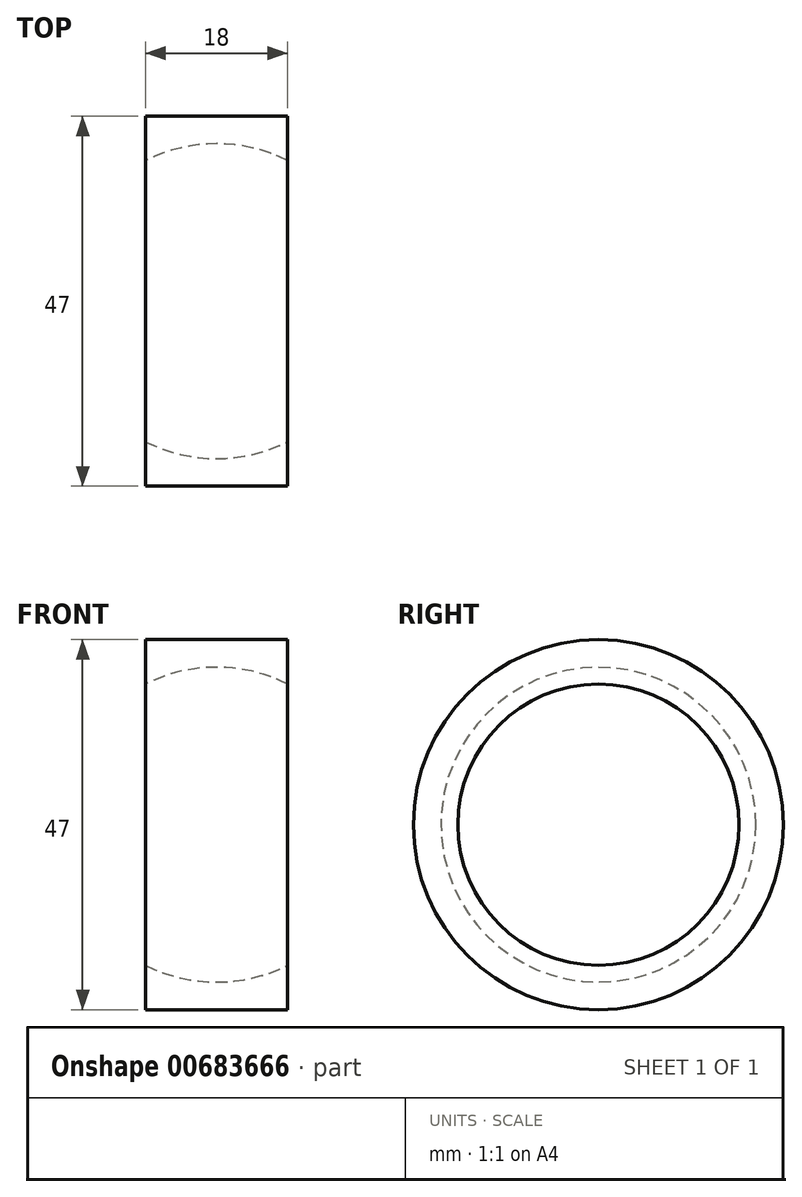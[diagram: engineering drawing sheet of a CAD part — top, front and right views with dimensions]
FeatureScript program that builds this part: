
annotation { "Feature Type Name" : "Feature", "Feature Type Description" : "" }
export const myFeature = defineFeature(function(context is Context, id is Id, definition is map)
    precondition{}
    {
        {
            var Q0;
            Q0=qCreatedBy(makeId("Front.planeOp"),FACE);
            var sketch = newSketch(context, id + "F0", { "sketchPlane" : qUnion([Q0])});
            skLineSegment(sketch, "E0", {"start": v(0, 23.5) * mm, "end": v(18, 23.5) * mm});
            skArc(sketch, "E1", {"start": v(18, 17.86) * mm, "mid": v(9, 20) * mm, "end": v(0, 17.86) * mm});
            skPoint(sketch, "E1.centerSnap0", {"position": v(9, 23.5) * mm});
            skLineSegment(sketch, "E2", {"start": v(0, 23.5) * mm, "end": v(0, 17.86) * mm});
            skLineSegment(sketch, "E3", {"start": v(18, 23.5) * mm, "end": v(18, 17.86) * mm});
            skLineSegment(sketch, "E4", {"start": v(0, 0) * mm, "end": v(17.22, 0) * mm, "construction": true});
            skSolve(sketch);
        }
        {
            var Q0;
            Q0=makeQuery(id+"F0.imprint","IMPRINT",FACE,{"disambiguationData":[TD([[makeQuery(id+"F0.imprint","IMPRINT",EDGE,{"derivedFrom":sQuery(id+"F0.wireOp",EDGE,"E0")}),-1.0]])]});
            var Q1;
            Q1=sQuery(id+"F0.wireOp",EDGE,"E4");
            revolve(context, id + "F1", {"entities" : qUnion([Q0]), "axis" : qUnion([Q1]), "revolveType" : RevolveType.FULL});
        }
    });
